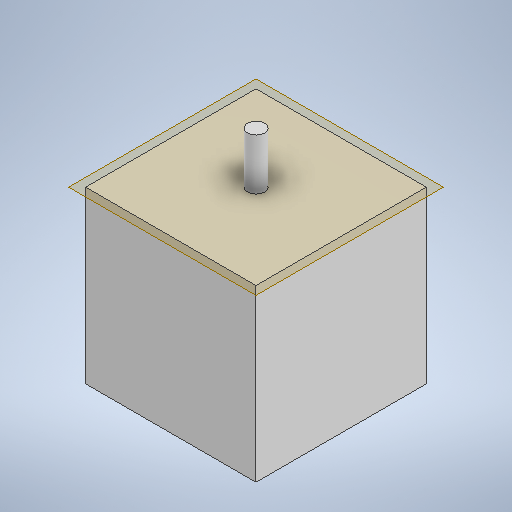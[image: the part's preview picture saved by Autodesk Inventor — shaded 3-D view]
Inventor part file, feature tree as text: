
AUTODESK INVENTOR PART (.ipt)
format: ipt  version: 2025.1 (Build 291241000, 241)  size: 205,312 bytes
history: native  units: mm
features: other x2, extrude x2, sketch x2
ambient origin geometry x8: Origin, YZ Plane, XZ Plane, XY Plane, X Axis, Y Axis, Z Axis, Center Point
bodies: Body1 (feature_tree)
feature tree (6):
  other  "ソリッド1"
  extrude  "押し出し1"  Depth=50.0mm
  other  "作業平面1"
  extrude  "押し出し2"  Depth=50.0mm
  sketch  "スケッチ1"
  sketch  "スケッチ2"
